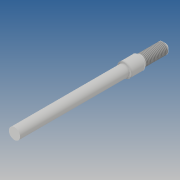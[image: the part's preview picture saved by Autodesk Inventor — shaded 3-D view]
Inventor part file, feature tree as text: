
AUTODESK INVENTOR PART (.ipt)
format: ipt  version: 2019 (Build 230136000, 136)  size: 90,624 bytes
history: native  units: mm
features: other x2, chamfer x1, sketch x1
ambient origin geometry x8: Origin, YZ Plane, XZ Plane, XY Plane, X Axis, Y Axis, Z Axis, Center Point
bodies: Body1 (feature_tree)
feature tree (4):
  other  "Révolution1"
  other  "Filetage1"
  chamfer  "Chanfrein1"  Distance=10.0mm
  sketch  "Esquisse2"
